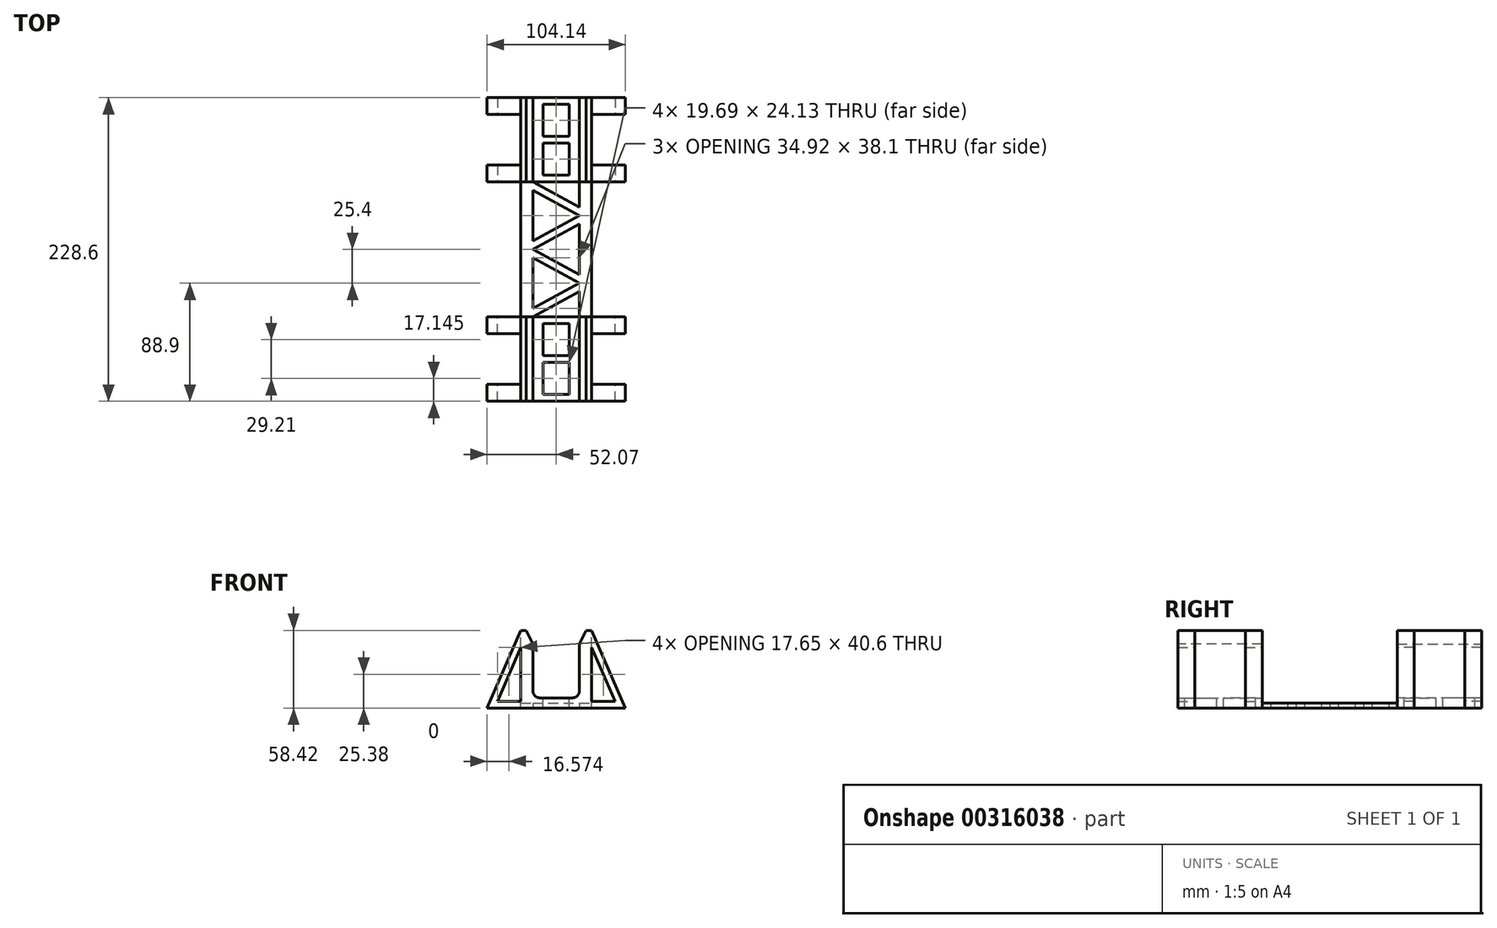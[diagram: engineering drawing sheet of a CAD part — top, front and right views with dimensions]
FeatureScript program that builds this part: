
annotation { "Feature Type Name" : "Feature", "Feature Type Description" : "" }
export const myFeature = defineFeature(function(context is Context, id is Id, definition is map)
    precondition{}
    {
        {
            var Q0;
            Q0=qCreatedBy(makeId("Front.planeOp"),FACE);
            var sketch = newSketch(context, id + "F0", { "sketchPlane" : qUnion([Q0])});
            skLineSegment(sketch, "E0.bottom", {"start": v(0, 0) * mm, "end": v(53.34, 0) * mm});
            skLineSegment(sketch, "E0.top", {"start": v(0, 58.42) * mm, "end": v(53.34, 58.42) * mm, "construction": true});
            skLineSegment(sketch, "E0.left", {"start": v(0, 0) * mm, "end": v(0, 58.42) * mm});
            skLineSegment(sketch, "E0.right", {"start": v(53.34, 0) * mm, "end": v(53.34, 58.42) * mm});
            skLineSegment(sketch, "E1", {"start": v(26.67, 0) * mm, "end": v(26.67, 58.42) * mm, "construction": true});
            skLineSegment(sketch, "E2", {"start": v(44.13, 58.42) * mm, "end": v(44.13, 7.62) * mm});
            skLineSegment(sketch, "E3", {"start": v(44.13, 7.62) * mm, "end": v(26.67, 7.62) * mm});
            skLineSegment(sketch, "E4.MirrorCS", {"start": v(9.2, 7.62) * mm, "end": v(26.67, 7.62) * mm});
            skLineSegment(sketch, "E5.MirrorCS", {"start": v(9.2, 58.42) * mm, "end": v(9.2, 7.62) * mm});
            skLineSegment(sketch, "E6", {"start": v(0, 58.42) * mm, "end": v(9.2, 58.42) * mm});
            skLineSegment(sketch, "E7", {"start": v(44.13, 58.42) * mm, "end": v(53.34, 58.42) * mm});
            skSolve(sketch);
        }
        {
            var Q0;
            Q0=makeQuery(id+"F0.imprint","IMPRINT",FACE,{"disambiguationData":[TD([[makeQuery(id+"F0.imprint","IMPRINT",EDGE,{"derivedFrom":sQuery(id+"F0.wireOp",EDGE,"E0.bottom")}),1.0]])]});
            extrude(context, id + "F1", {"entities" : qUnion([Q0]), "depth" : 114.3 * mm});
        }
        {
            var Q0;
            Q0=qCreatedBy(makeId("Front.planeOp"),FACE);
            var sketch = newSketch(context, id + "F2", { "sketchPlane" : qUnion([Q0])});
            skLineSegment(sketch, "E8", {"start": v(0, 0) * mm, "end": v(-25.4, 0) * mm});
            skLineSegment(sketch, "E9.0", {"start": v(0, 0) * mm, "end": v(0, 58.42) * mm});
            skLineSegment(sketch, "E10", {"start": v(0, 58.42) * mm, "end": v(-25.4, 0) * mm});
            skLineSegment(sketch, "E11.MirrorCS", {"start": v(53.34, 58.42) * mm, "end": v(78.74, 0) * mm});
            skLineSegment(sketch, "E12.MirrorCS", {"start": v(53.34, 0) * mm, "end": v(53.34, 58.42) * mm});
            skLineSegment(sketch, "E13.MirrorCS", {"start": v(53.34, 0) * mm, "end": v(78.74, 0) * mm});
            skLineSegment(sketch, "E14.0", {"start": v(0, 45.68) * mm, "end": v(-17.65, 5.08) * mm});
            skLineSegment(sketch, "E14.2", {"start": v(0, 5.08) * mm, "end": v(-17.65, 5.08) * mm});
            skLineSegment(sketch, "E15.0", {"start": v(53.34, 45.68) * mm, "end": v(71, 5.08) * mm});
            skLineSegment(sketch, "E15.2", {"start": v(53.34, 5.08) * mm, "end": v(71, 5.08) * mm});
            skSolve(sketch);
        }
        {
            var Q0;
            Q0=makeQuery(id+"F2.imprint","IMPRINT",FACE,{"disambiguationData":[TD([[makeQuery(id+"F2.imprint","IMPRINT",EDGE,{"derivedFrom":sQuery(id+"F2.wireOp",EDGE,"E11.MirrorCS")}),-1.0]])]});
            var Q1;
            Q1=makeQuery(id+"F2.imprint","IMPRINT",FACE,{"disambiguationData":[TD([[makeQuery(id+"F2.imprint","IMPRINT",EDGE,{"derivedFrom":sQuery(id+"F2.wireOp",EDGE,"E8")}),-1.0]])]});
            extrude(context, id + "F3", {"entities" : qUnion([Q0, Q1]), "operationType" : NewBodyOperationType.ADD, "depth" : 114.3 * mm, "hasSecondDirection" : true, "secondDirectionOppositeDirection" : false, "secondDirectionDepth" : 101.6 * mm});
        }
        {
            var Q0;
            {var subQ2=sQuery(id+"F2.wireOp",EDGE,"E11.MirrorCS");Q0=makeQuery(id+"F2.imprint","IMPRINT",FACE,{"disambiguationData":[TD([[makeQuery(id+"F2.imprint","IMPRINT",EDGE,{"derivedFrom":subQ2}),-1.0]])]});}
            var Q1;
            {var subQ3=sQuery(id+"F2.wireOp",EDGE,"E8");Q1=makeQuery(id+"F2.imprint","IMPRINT",FACE,{"disambiguationData":[TD([[makeQuery(id+"F2.imprint","IMPRINT",EDGE,{"derivedFrom":subQ3}),-1.0]])]});}
            extrude(context, id + "F4", {"entities" : qUnion([Q0, Q1]), "operationType" : NewBodyOperationType.ADD, "depth" : 63.5 * mm, "hasSecondDirection" : true, "secondDirectionOppositeDirection" : false, "secondDirectionDepth" : 50.8 * mm});
        }
        {
            var Q0;
            Q0=qCreatedBy(makeId("Top.planeOp"),FACE);
            var sketch = newSketch(context, id + "F5", { "sketchPlane" : qUnion([Q0])});
            skPoint(sketch, "E16.0", {"position": v(53.34, -50.8) * mm});
            skPoint(sketch, "E16.1", {"position": v(0, -50.8) * mm});
            skPoint(sketch, "E16.2", {"position": v(0, 0) * mm});
            skPoint(sketch, "E16.3", {"position": v(53.34, 0) * mm});
            skLineSegment(sketch, "E17.bottom", {"start": v(0, 0) * mm, "end": v(53.34, 0) * mm});
            skLineSegment(sketch, "E17.top", {"start": v(0, -50.8) * mm, "end": v(53.34, -50.8) * mm});
            skLineSegment(sketch, "E17.left", {"start": v(0, 0) * mm, "end": v(0, -50.8) * mm});
            skLineSegment(sketch, "E17.right", {"start": v(53.34, 0) * mm, "end": v(53.34, -50.8) * mm});
            skSolve(sketch);
        }
        {
            var Q0;
            Q0=makeQuery(id+"F5.imprint","IMPRINT",FACE,{"disambiguationData":[TD([[makeQuery(id+"F5.imprint","IMPRINT",EDGE,{"derivedFrom":sQuery(id+"F5.wireOp",EDGE,"E17.bottom")}),-1.0]])]});
            var Q1;
            Q1=makeQuery(id+"F1.opExtrude","SWEPT_FACE",FACE,{"disambiguationData":[OSD([sQuery(id+"F0.wireOp",EDGE,"E7")])]});
            var Q2;
            Q2=makeQuery(id+"F1.opExtrude","SWEPT_FACE",FACE,{"disambiguationData":[OSD([sQuery(id+"F0.wireOp",EDGE,"E3"),sQuery(id+"F0.wireOp",EDGE,"E4.MirrorCS")])]});
            extrude(context, id + "F6", {"entities" : qUnion([Q0]), "operationType" : NewBodyOperationType.REMOVE, "endBound" : BoundingType.UP_TO_SURFACE, "endBoundEntityFace" : qUnion([Q1]), "depth" : 25.4 * mm, "hasSecondDirection" : true, "secondDirectionOppositeDirection" : false, "secondDirectionBoundEntityFace" : qUnion([Q2]), "secondDirectionDepth" : 3.8 * mm});
        }
        {
            var Q0;
            Q0=makeQuery(id+"F5.imprint","IMPRINT",FACE,{"disambiguationData":[TD([[makeQuery(id+"F5.imprint","IMPRINT",EDGE,{"derivedFrom":sQuery(id+"F5.wireOp",EDGE,"E17.bottom")}),-1.0]])]});
            var sketch = newSketch(context, id + "F7", { "sketchPlane" : qUnion([Q0])});
            skPoint(sketch, "E18.0", {"position": v(0, -50.8) * mm});
            skPoint(sketch, "E18.1", {"position": v(53.34, -50.8) * mm});
            skPoint(sketch, "E18.2", {"position": v(53.34, 0) * mm});
            skPoint(sketch, "E18.3", {"position": v(44.13, 0) * mm});
            skPoint(sketch, "E18.4", {"position": v(9.2, 0) * mm});
            skPoint(sketch, "E18.5", {"position": v(0, 0) * mm});
            skLineSegment(sketch, "E19", {"start": v(53.34, -50.8) * mm, "end": v(0, -50.8) * mm, "construction": true});
            skLineSegment(sketch, "E20.bottom", {"start": v(9.2, 0) * mm, "end": v(44.13, 0) * mm, "construction": true});
            skLineSegment(sketch, "E20.top", {"start": v(9.2, -50.8) * mm, "end": v(44.13, -50.8) * mm, "construction": true});
            skLineSegment(sketch, "E20.left", {"start": v(9.2, 0) * mm, "end": v(9.2, -50.8) * mm, "construction": true});
            skLineSegment(sketch, "E20.right", {"start": v(44.13, 0) * mm, "end": v(44.13, -50.8) * mm, "construction": true});
            skPoint(sketch, "E21", {"position": v(44.13, -25.4) * mm});
            skLineSegment(sketch, "E22", {"start": v(9.2, 0) * mm, "end": v(9.2, -6.35) * mm, "construction": true});
            skLineSegment(sketch, "E23", {"start": v(9.2, -6.35) * mm, "end": v(44.13, -25.4) * mm});
            skLineSegment(sketch, "E24", {"start": v(9.2, 0) * mm, "end": v(9.2, 0) * mm});
            skLineSegment(sketch, "E25", {"start": v(9.2, 0) * mm, "end": v(44.13, -19.05) * mm});
            skLineSegment(sketch, "E26", {"start": v(44.13, -19.05) * mm, "end": v(44.13, -25.4) * mm, "construction": true});
            skLineSegment(sketch, "E27", {"start": v(44.13, -25.4) * mm, "end": v(9.2, -25.4) * mm, "construction": true});
            skLineSegment(sketch, "E28.MirrorCS", {"start": v(9.2, -44.45) * mm, "end": v(44.13, -25.4) * mm});
            skLineSegment(sketch, "E29.MirrorCS", {"start": v(9.2, -50.8) * mm, "end": v(44.13, -31.75) * mm});
            skLineSegment(sketch, "E30.MirrorCS", {"start": v(9.2, -50.8) * mm, "end": v(9.2, -50.8) * mm});
            skLineSegment(sketch, "E31.MirrorCS", {"start": v(9.2, -50.8) * mm, "end": v(9.2, -44.45) * mm, "construction": true});
            skPoint(sketch, "E32.MirrorP", {"position": v(9.2, -50.8) * mm});
            skLineSegment(sketch, "E33.MirrorCS", {"start": v(44.13, -31.75) * mm, "end": v(44.13, -25.4) * mm, "construction": true});
            skLineSegment(sketch, "E34.MirrorCS", {"start": v(44.13, -50.8) * mm, "end": v(44.13, 0) * mm, "construction": true});
            skLineSegment(sketch, "E35", {"start": v(9.2, -50.8) * mm, "end": v(0, -50.8) * mm});
            skLineSegment(sketch, "E36", {"start": v(0, 0) * mm, "end": v(9.2, 0) * mm, "construction": true});
            skLineSegment(sketch, "E37", {"start": v(9.2, -6.35) * mm, "end": v(9.2, -44.45) * mm, "construction": true});
            skLineSegment(sketch, "E38", {"start": v(44.13, -19.05) * mm, "end": v(44.13, 0) * mm});
            skLineSegment(sketch, "E39", {"start": v(9.2, 0) * mm, "end": v(44.13, 0) * mm});
            skLineSegment(sketch, "E40", {"start": v(9.2, -6.35) * mm, "end": v(9.2, -44.45) * mm});
            skLineSegment(sketch, "E41", {"start": v(9.2, -50.8) * mm, "end": v(44.13, -50.8) * mm});
            skLineSegment(sketch, "E42", {"start": v(44.13, -31.75) * mm, "end": v(44.13, -50.8) * mm});
            skSolve(sketch);
        }
        {
            var Q0;
            Q0=makeQuery(id+"F7.imprint","IMPRINT",FACE,{"disambiguationData":[TD([[makeQuery(id+"F7.imprint","IMPRINT",EDGE,{"derivedFrom":sQuery(id+"F7.wireOp",EDGE,"E29.MirrorCS")}),-1.0]])]});
            var Q1;
            Q1=makeQuery(id+"F7.imprint","IMPRINT",FACE,{"disambiguationData":[TD([[makeQuery(id+"F7.imprint","IMPRINT",EDGE,{"derivedFrom":sQuery(id+"F7.wireOp",EDGE,"E23")}),-1.0]])]});
            var Q2;
            Q2=makeQuery(id+"F7.imprint","IMPRINT",FACE,{"disambiguationData":[TD([[makeQuery(id+"F7.imprint","IMPRINT",EDGE,{"derivedFrom":sQuery(id+"F7.wireOp",EDGE,"E25")}),1.0]])]});
            var Q3;
            Q3=makeQuery(id+"F6.boolean.opBoolean","COPY",FACE,{"derivedFrom":makeQuery(id+"F6.opExtrude","CAP_FACE",FACE,{"disambiguationData":[OSD([sQuery(id+"F5.wireOp",EDGE,"E17.bottom"),sQuery(id+"F5.wireOp",EDGE,"E17.top"),sQuery(id+"F5.wireOp",EDGE,"E17.left"),sQuery(id+"F5.wireOp",EDGE,"E17.right")])],"isStart":true})});
            extrude(context, id + "F8", {"entities" : qUnion([Q0, Q1, Q2]), "operationType" : NewBodyOperationType.REMOVE, "endBound" : BoundingType.UP_TO_SURFACE, "endBoundEntityFace" : qUnion([Q3]), "depth" : 25.4 * mm});
        }
        {
            var Q0;
            Q0=makeQuery(id+"F1.opExtrude","SWEPT_EDGE",EDGE,{"disambiguationData":[OSD([sQuery(id+"F0.wireOp",EDGE,"E4.MirrorCS"),sQuery(id+"F0.wireOp",EDGE,"E5.MirrorCS")])]});
            var Q1;
            Q1=makeQuery(id+"F1.opExtrude","SWEPT_EDGE",EDGE,{"disambiguationData":[OSD([sQuery(id+"F0.wireOp",EDGE,"E2"),sQuery(id+"F0.wireOp",EDGE,"E3")])]});
            fillet(context, id + "F9", {"entities" : qUnion([Q0, Q1]), "radius" : 5.08 * mm, "tangentPropagation" : true, "allowEdgeOverflow" : false});
        }
        {
            var Q0;
            Q0=makeQuery(id+"F1.opExtrude","SWEPT_EDGE",EDGE,{"disambiguationData":[OSD([sQuery(id+"F0.wireOp",EDGE,"E5.MirrorCS"),sQuery(id+"F0.wireOp",EDGE,"E6")])]});
            chamfer(context, id + "F10", {"entities" : qUnion([Q0]), "chamferType" : ChamferType.TWO_OFFSETS, "width1" : 5.08 * mm, "oppositeDirection" : false, "width2" : 10.16 * mm, "tangentPropagation" : true});
        }
        {
            var Q0;
            Q0=makeQuery(id+"F1.opExtrude","SWEPT_EDGE",EDGE,{"disambiguationData":[OSD([sQuery(id+"F0.wireOp",EDGE,"E2"),sQuery(id+"F0.wireOp",EDGE,"E7")])]});
            chamfer(context, id + "F11", {"entities" : qUnion([Q0]), "chamferType" : ChamferType.TWO_OFFSETS, "width1" : 10.16 * mm, "oppositeDirection" : false, "width2" : 5.08 * mm, "tangentPropagation" : true});
        }
        {
            var Q0;
            Q0=makeQuery(id+"F1.opExtrude","SWEPT_FACE",FACE,{"disambiguationData":[OSD([sQuery(id+"F0.wireOp",EDGE,"E3"),sQuery(id+"F0.wireOp",EDGE,"E4.MirrorCS")])]});
            var sketch = newSketch(context, id + "F12", { "sketchPlane" : qUnion([Q0])});
            skLineSegment(sketch, "E43.0.0", {"start": v(14.29, -114.3) * mm, "end": v(39.05, -114.3) * mm, "construction": true});
            skLineSegment(sketch, "E43.0.1", {"start": v(39.05, -114.3) * mm, "end": v(39.05, -50.8) * mm, "construction": true});
            skLineSegment(sketch, "E43.0.2", {"start": v(39.05, -50.8) * mm, "end": v(14.29, -50.8) * mm, "construction": true});
            skLineSegment(sketch, "E43.0.3", {"start": v(14.29, -50.8) * mm, "end": v(14.29, -114.3) * mm, "construction": true});
            skPoint(sketch, "E44", {"position": v(14.29, -82.55) * mm});
            skPoint(sketch, "E45", {"position": v(39.05, -82.55) * mm});
            skLineSegment(sketch, "E46", {"start": v(14.29, -82.55) * mm, "end": v(39.05, -82.55) * mm, "construction": true});
            skLineSegment(sketch, "E47.bottom", {"start": v(16.83, -55.88) * mm, "end": v(36.51, -55.88) * mm});
            skLineSegment(sketch, "E47.top", {"start": v(16.83, -80.01) * mm, "end": v(36.51, -80.01) * mm});
            skLineSegment(sketch, "E47.left", {"start": v(16.83, -55.88) * mm, "end": v(16.83, -80.01) * mm});
            skLineSegment(sketch, "E47.right", {"start": v(36.51, -55.88) * mm, "end": v(36.51, -80.01) * mm});
            skLineSegment(sketch, "E48.MirrorCS", {"start": v(16.83, -85.1) * mm, "end": v(36.51, -85.1) * mm});
            skLineSegment(sketch, "E49.MirrorCS", {"start": v(36.51, -109.22) * mm, "end": v(36.51, -85.1) * mm});
            skLineSegment(sketch, "E50.MirrorCS", {"start": v(16.83, -109.22) * mm, "end": v(16.83, -85.1) * mm});
            skLineSegment(sketch, "E51.MirrorCS", {"start": v(16.83, -109.22) * mm, "end": v(36.51, -109.22) * mm});
            skSolve(sketch);
        }
        {
            var Q0;
            Q0 = qSketchRegion(id + "F12", true);
            var Q1;
            Q1=makeQuery(id+"F12.imprint","IMPRINT",FACE,{"disambiguationData":[TD([[makeQuery(id+"F12.imprint","IMPRINT",EDGE,{"derivedFrom":sQuery(id+"F12.wireOp",EDGE,"E47.bottom")}),-1.0]])]});
            extrude(context, id + "F13", {"entities" : qUnion([Q0, Q1]), "operationType" : NewBodyOperationType.REMOVE, "endBound" : BoundingType.UP_TO_NEXT, "oppositeDirection" : true, "depth" : 25.4 * mm});
        }
        {
            var Q0;
            Q0=makeQuery(id+"F1.opExtrude","SWEPT_BODY",BODY,{"disambiguationData":[OSD([sQuery(id+"F0.wireOp",EDGE,"E0.bottom"),sQuery(id+"F0.wireOp",EDGE,"E0.left"),sQuery(id+"F0.wireOp",EDGE,"E0.right"),sQuery(id+"F0.wireOp",EDGE,"E2"),sQuery(id+"F0.wireOp",EDGE,"E3"),sQuery(id+"F0.wireOp",EDGE,"E4.MirrorCS"),sQuery(id+"F0.wireOp",EDGE,"E5.MirrorCS"),sQuery(id+"F0.wireOp",EDGE,"E6"),sQuery(id+"F0.wireOp",EDGE,"E7")])]});
            var Q1;
            Q1=qCreatedBy(makeId("Front.planeOp"),FACE);
            mirror(context, id + "F14", {"operationType" : NewBodyOperationType.ADD, "entities" : qUnion([Q0]), "mirrorPlane" : qUnion([Q1])});
        }
    });
